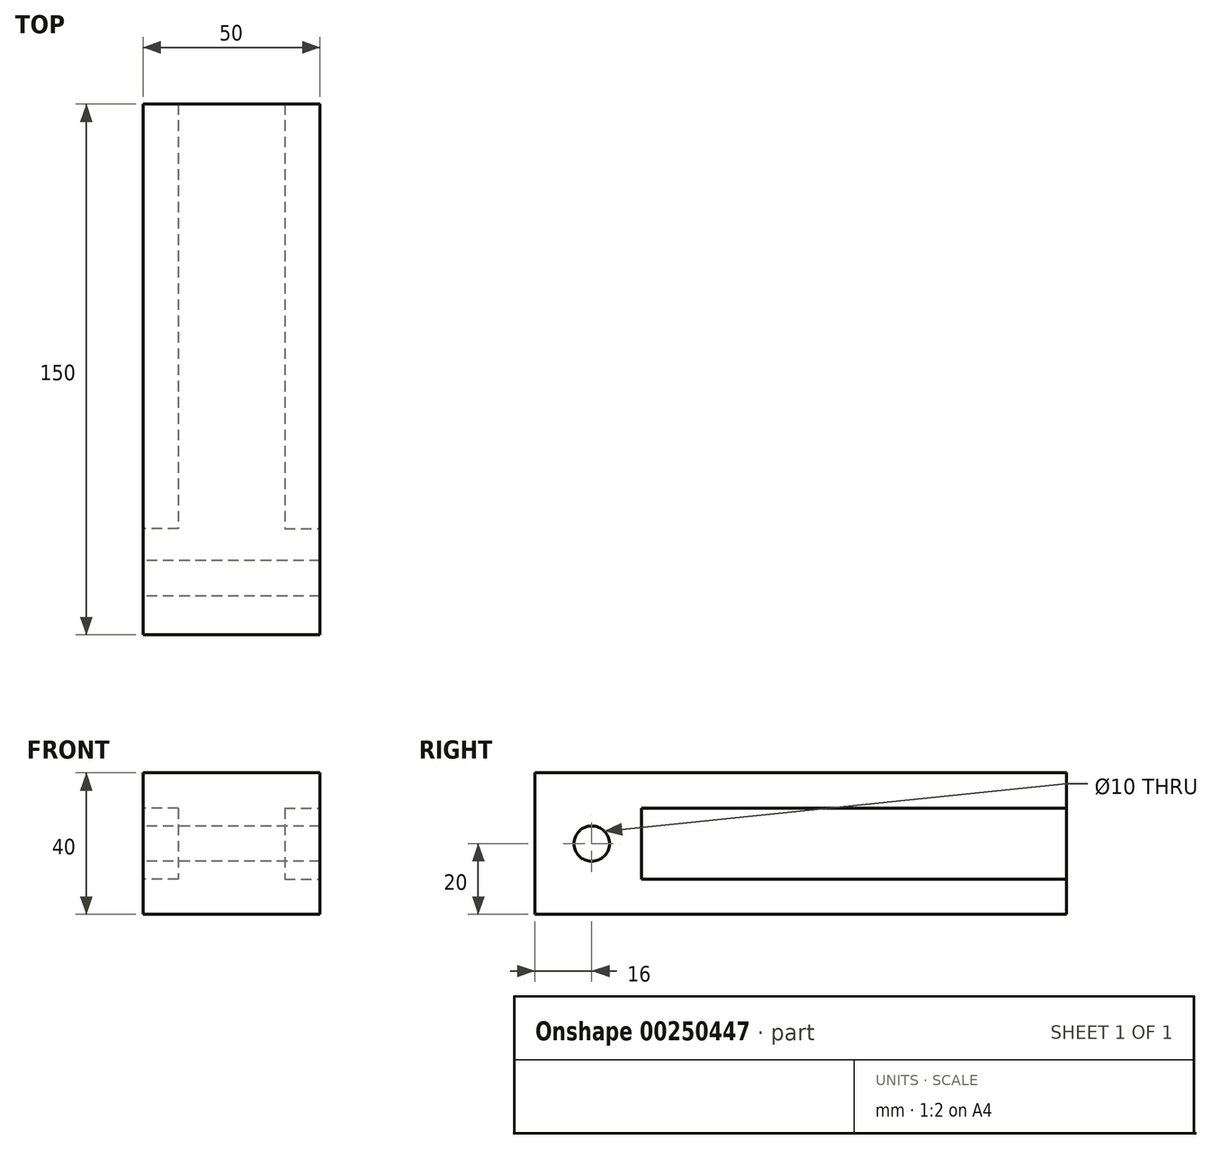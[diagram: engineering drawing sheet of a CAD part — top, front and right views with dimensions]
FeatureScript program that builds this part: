
annotation { "Feature Type Name" : "Feature", "Feature Type Description" : "" }
export const myFeature = defineFeature(function(context is Context, id is Id, definition is map)
    precondition{}
    {
        {
            var Q0;
            Q0=qCreatedBy(makeId("Front.planeOp"),FACE);
            var sketch = newSketch(context, id + "F0", { "sketchPlane" : qUnion([Q0])});
            skLineSegment(sketch, "E0.bottom", {"start": v(25, 20) * mm, "end": v(-25, 20) * mm});
            skLineSegment(sketch, "E0.top", {"start": v(25, -20) * mm, "end": v(-25, -20) * mm});
            skLineSegment(sketch, "E0.left", {"start": v(25, 20) * mm, "end": v(25, -20) * mm});
            skLineSegment(sketch, "E0.right", {"start": v(-25, 20) * mm, "end": v(-25, -20) * mm});
            skPoint(sketch, "E0.middle", {"position": v(0, 0) * mm});
            skSolve(sketch);
        }
        {
            var Q0;
            Q0=makeQuery(id+"F0.imprint","IMPRINT",FACE,{"disambiguationData":[TD([[makeQuery(id+"F0.imprint","IMPRINT",EDGE,{"derivedFrom":sQuery(id+"F0.wireOp",EDGE,"E0.bottom")}),1.0]])]});
            extrude(context, id + "F1", {"entities" : qUnion([Q0]), "depth" : 150 * mm});
        }
        {
            var Q0;
            Q0=makeQuery(id+"F1.opExtrude","SWEPT_FACE",FACE,{"disambiguationData":[OSD([sQuery(id+"F0.wireOp",EDGE,"E0.left")])]});
            var sketch = newSketch(context, id + "F2", { "sketchPlane" : qUnion([Q0])});
            skLineSegment(sketch, "E1", {"start": v(0, 10) * mm, "end": v(-120, 10) * mm});
            skLineSegment(sketch, "E2", {"start": v(-120, 10) * mm, "end": v(-120, -10) * mm});
            skLineSegment(sketch, "E3", {"start": v(-120, -10) * mm, "end": v(0, -10) * mm});
            skLineSegment(sketch, "E4", {"start": v(0, 10) * mm, "end": v(0, -10) * mm});
            skSolve(sketch);
        }
        {
            var Q0;
            Q0=makeQuery(id+"F2.imprint","IMPRINT",FACE,{"disambiguationData":[TD([[makeQuery(id+"F2.imprint","IMPRINT",EDGE,{"derivedFrom":sQuery(id+"F2.wireOp",EDGE,"E1")}),1.0]])]});
            extrude(context, id + "F3", {"entities" : qUnion([Q0]), "oppositeDirection" : true, "depth" : 10 * mm});
        }
        {
            var Q0;
            Q0=makeQuery(id+"F3.opExtrude","SWEPT_BODY",BODY,{"disambiguationData":[OSD([sQuery(id+"F2.wireOp",EDGE,"E1"),sQuery(id+"F2.wireOp",EDGE,"E2"),sQuery(id+"F2.wireOp",EDGE,"E3"),sQuery(id+"F2.wireOp",EDGE,"E4")])]});
            var Q1;
            Q1=makeQuery(id+"F1.opExtrude","SWEPT_BODY",BODY,{"disambiguationData":[OSD([sQuery(id+"F0.wireOp",EDGE,"E0.bottom"),sQuery(id+"F0.wireOp",EDGE,"E0.top"),sQuery(id+"F0.wireOp",EDGE,"E0.left"),sQuery(id+"F0.wireOp",EDGE,"E0.right")])]});
            booleanBodies(context, id + "F4", {"operationType" : BooleanOperationType.SUBTRACTION, "tools" : qUnion([Q0]), "targets" : qUnion([Q1])});
        }
        {
            var Q0;
            Q0=makeQuery(id+"F1.opExtrude","SWEPT_FACE",FACE,{"disambiguationData":[OSD([sQuery(id+"F0.wireOp",EDGE,"E0.right")])]});
            var sketch = newSketch(context, id + "F5", { "sketchPlane" : qUnion([Q0])});
            skLineSegment(sketch, "E5.bottom", {"start": v(0, -10) * mm, "end": v(120, -10) * mm});
            skLineSegment(sketch, "E5.top", {"start": v(0, 10) * mm, "end": v(120, 10) * mm});
            skLineSegment(sketch, "E5.left", {"start": v(0, -10) * mm, "end": v(0, 10) * mm});
            skLineSegment(sketch, "E5.right", {"start": v(120, -10) * mm, "end": v(120, 10) * mm});
            skSolve(sketch);
        }
        {
            var Q0;
            Q0=makeQuery(id+"F5.imprint","IMPRINT",FACE,{"disambiguationData":[TD([[makeQuery(id+"F5.imprint","IMPRINT",EDGE,{"derivedFrom":sQuery(id+"F5.wireOp",EDGE,"E5.bottom")}),1.0]])]});
            extrude(context, id + "F6", {"entities" : qUnion([Q0]), "oppositeDirection" : true, "depth" : 10 * mm});
        }
        {
            var Q0;
            Q0=makeQuery(id+"F6.opExtrude","SWEPT_BODY",BODY,{"disambiguationData":[OSD([sQuery(id+"F5.wireOp",EDGE,"E5.bottom"),sQuery(id+"F5.wireOp",EDGE,"E5.top"),sQuery(id+"F5.wireOp",EDGE,"E5.left"),sQuery(id+"F5.wireOp",EDGE,"E5.right")])]});
            var Q1;
            Q1=makeQuery(id+"F1.opExtrude","SWEPT_BODY",BODY,{"disambiguationData":[OSD([sQuery(id+"F0.wireOp",EDGE,"E0.bottom"),sQuery(id+"F0.wireOp",EDGE,"E0.top"),sQuery(id+"F0.wireOp",EDGE,"E0.left"),sQuery(id+"F0.wireOp",EDGE,"E0.right")])]});
            booleanBodies(context, id + "F7", {"operationType" : BooleanOperationType.SUBTRACTION, "tools" : qUnion([Q0]), "targets" : qUnion([Q1])});
        }
        {
            var Q0;
            Q0=makeQuery(id+"F1.opExtrude","SWEPT_FACE",FACE,{"disambiguationData":[OSD([sQuery(id+"F0.wireOp",EDGE,"E0.right")])]});
            var sketch = newSketch(context, id + "F8", { "sketchPlane" : qUnion([Q0])});
            skCircle(sketch, "E6", {"center": v(134, 0) * mm, "radius": 5 * mm});
            skSolve(sketch);
        }
        {
            var Q0;
            Q0=makeQuery(id+"F8.imprint","IMPRINT",FACE,{"disambiguationData":[TD([[makeQuery(id+"F8.imprint","IMPRINT",EDGE,{"derivedFrom":sQuery(id+"F8.wireOp",EDGE,"E6")}),1.0]])]});
            var Q1;
            Q1=sQuery(id+"F8.wireOp",EDGE,"E6");
            extrude(context, id + "F9", {"entities" : qUnion([Q0]), "surfaceEntities" : qUnion([Q1]), "oppositeDirection" : true, "depth" : 60 * mm});
        }
        {
            var Q0;
            Q0=makeQuery(id+"F9.opExtrude","SWEPT_BODY",BODY,{"disambiguationData":[OSD([sQuery(id+"F8.wireOp",EDGE,"E6")])]});
            var Q1;
            Q1=makeQuery(id+"F1.opExtrude","SWEPT_BODY",BODY,{"disambiguationData":[OSD([sQuery(id+"F0.wireOp",EDGE,"E0.bottom"),sQuery(id+"F0.wireOp",EDGE,"E0.top"),sQuery(id+"F0.wireOp",EDGE,"E0.left"),sQuery(id+"F0.wireOp",EDGE,"E0.right")])]});
            booleanBodies(context, id + "F10", {"operationType" : BooleanOperationType.SUBTRACTION, "tools" : qUnion([Q0]), "targets" : qUnion([Q1])});
        }
    });
